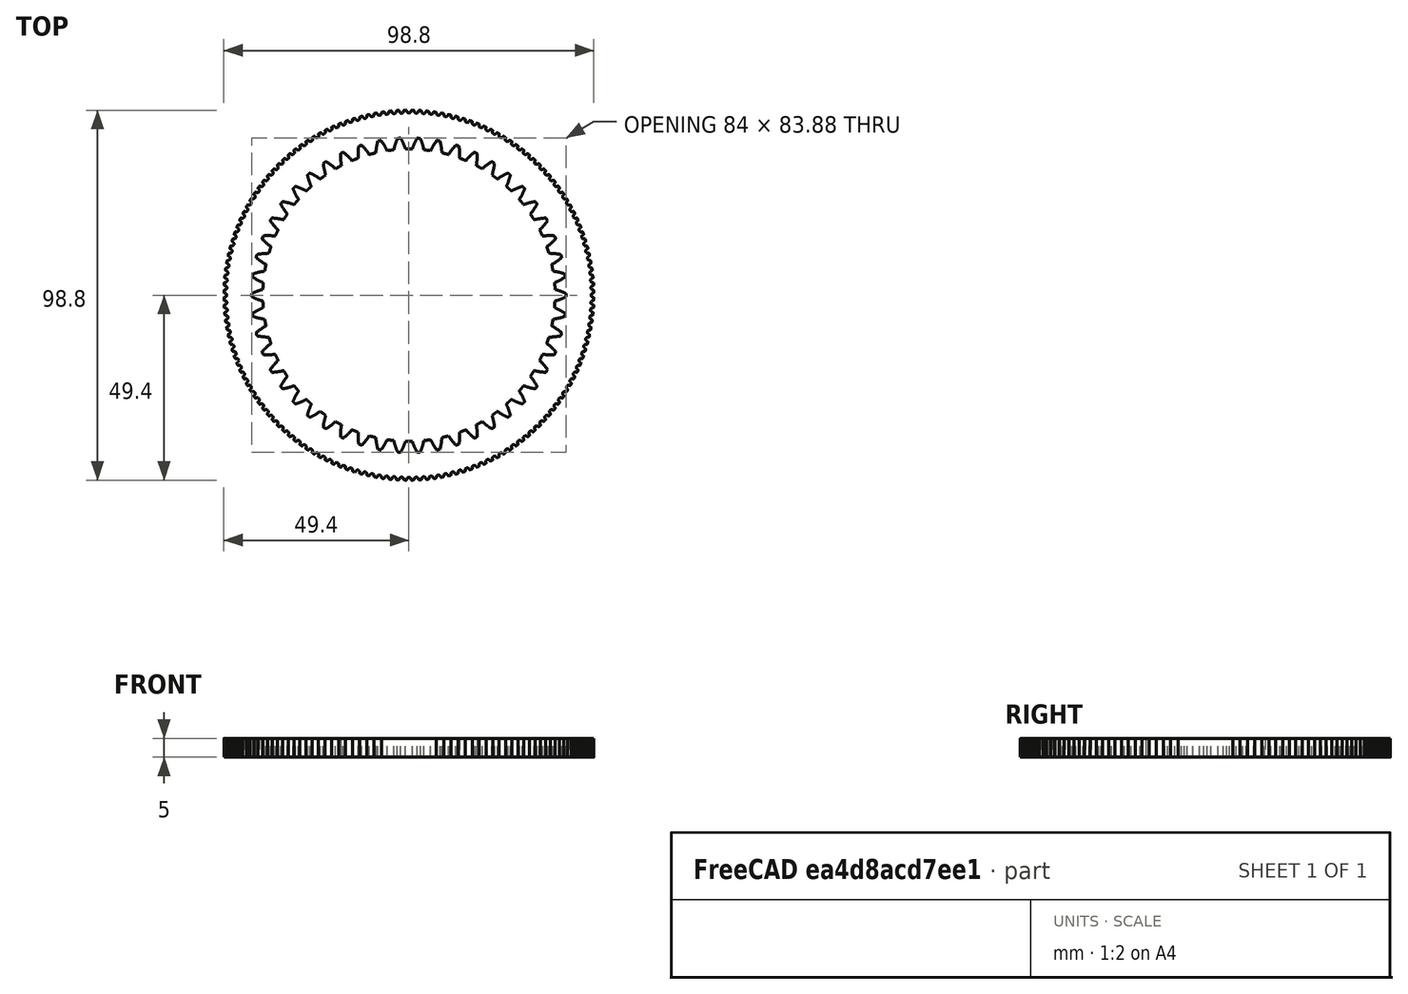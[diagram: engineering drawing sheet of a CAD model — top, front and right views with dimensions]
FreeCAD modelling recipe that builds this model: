
FCSTD DOCUMENT  (FreeCAD 0.20R29603 (Git))
Label: ring_gear_GT2_outer
License: All rights reserved
LicenseURL: http://en.wikipedia.org/wiki/All_rights_reserved
objects: Part::FeaturePython×2, Part::MultiCommon×1
note: 3 computed .brp shape members not serialized (recipe doc carries the construction recipe); baked Part::Feature solids carry a one-line shape summary decoded from their .brp

FEATURE [Part::FeaturePython] TimingGear  # WARN: FeaturePython — macro-defined, semantics opaque (R4)
  AttacherType = Attacher::AttachEngine3D
  h = 0.75
  height = 5
  offset = 0.4
  pitch = 2
  r0 = 0.555
  r1 = 1
  rs = 0.15
  teeth = 156
  type = 0
  u = 0.254
  version = 0.0.4
FEATURE [Part::FeaturePython] InternalInvoluteGear  # WARN: FeaturePython — macro-defined, semantics opaque (R4)
  AttacherType = Attacher::AttachEngine3D
  angular_backlash = 0
  backlash = 0
  beta = 0
  clearance = 0.25
  da = 78.08
  df = 84
  double_helix = false
  dw = 80
  head = -0.4
  head_fillet = 0
  height = 5
  module = 1.6
  numpoints = 6
  outside_diameter = 100
  pressure_angle = 20
  properties_from_tool = false
  reversed_backlash = false
  root_fillet = 0
  shift = 0
  simple = false
  teeth = 50
  thickness = 10
  transverse_pitch = 5.02655
  version = 0.0.4
  expr: angular_backlash = backlash / dw * 360° / pi
FEATURE [Part::MultiCommon] Common
  Shapes = -> [InternalInvoluteGear,TimingGear]
